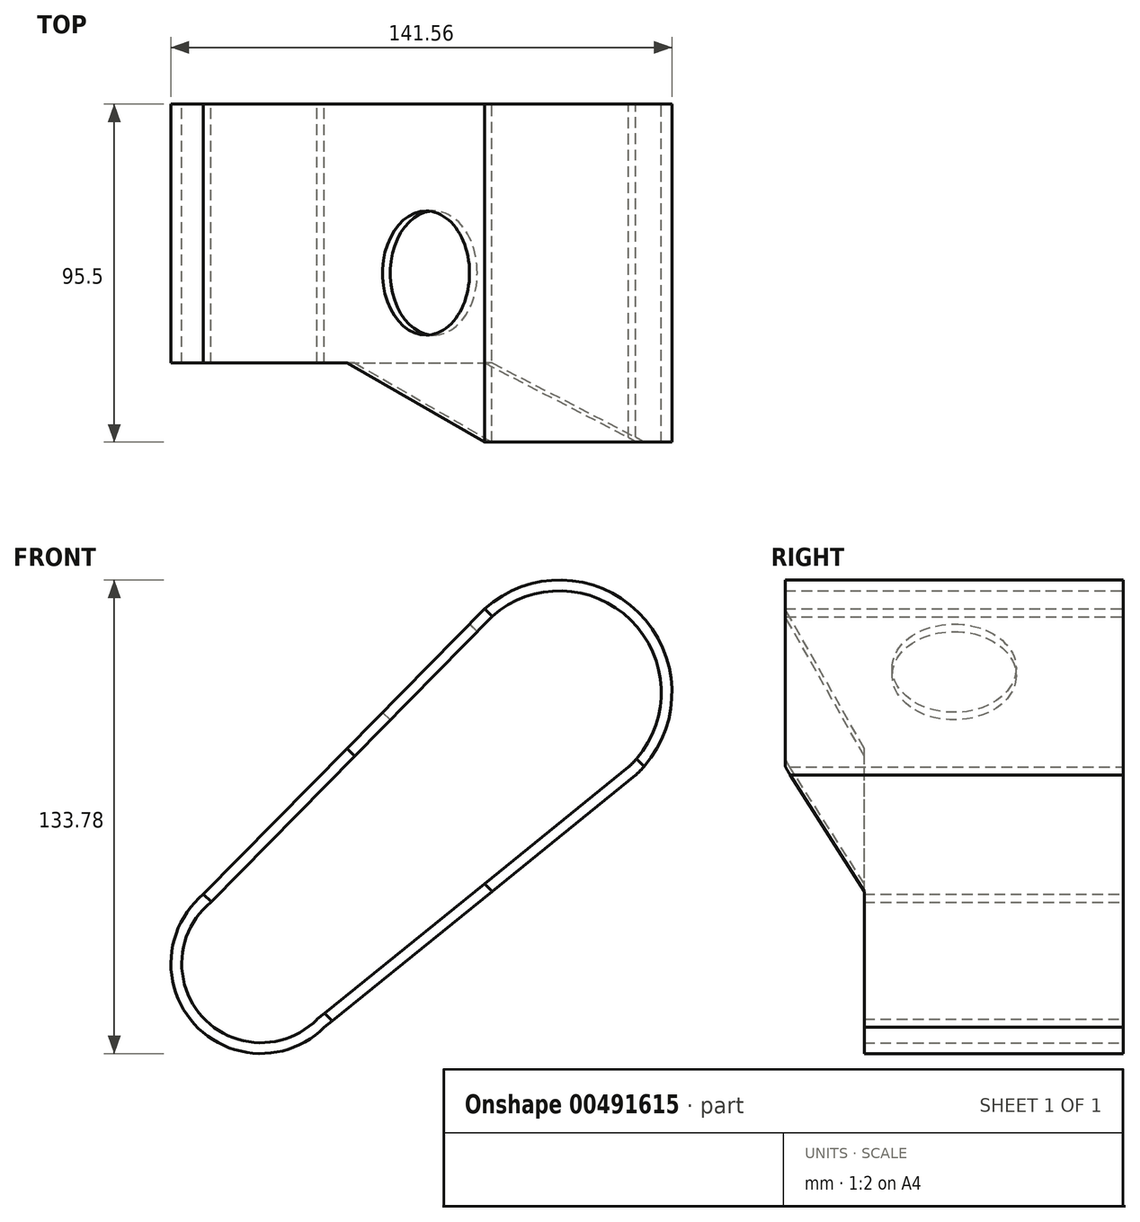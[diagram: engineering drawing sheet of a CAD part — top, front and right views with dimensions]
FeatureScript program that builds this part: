
annotation { "Feature Type Name" : "Feature", "Feature Type Description" : "" }
export const myFeature = defineFeature(function(context is Context, id is Id, definition is map)
    precondition{}
    {
        {
            var Q0;
            Q0=qCreatedBy(makeId("Front.planeOp"),FACE);
            var sketch = newSketch(context, id + "F0", { "sketchPlane" : qUnion([Q0])});
            skPoint(sketch, "E0.visualSharp", {"position": v(-73.61, -25.13) * mm});
            skPoint(sketch, "E1.visualSharp", {"position": v(-33.06, -65.08) * mm});
            skPoint(sketch, "E2.visualSharp", {"position": v(65.09, 34.55) * mm});
            skPoint(sketch, "E3.visualSharp", {"position": v(24.53, 74.5) * mm});
            skArc(sketch, "E4.1", {"start": v(-27.4, -54.87) * mm, "mid": v(-64.13, -53.94) * mm, "end": v(-61.56, -17.28) * mm});
            skArc(sketch, "E4.5", {"start": v(17.82, 63.36) * mm, "mid": v(62.56, 61.12) * mm, "end": v(60.53, 16.37) * mm});
            skLineSegment(sketch, "E5", {"start": v(-61.56, -17.28) * mm, "end": v(17.82, 63.36) * mm});
            skLineSegment(sketch, "E6", {"start": v(-27.4, -54.87) * mm, "end": v(60.53, 16.37) * mm});
            skLineSegment(sketch, "E7.0", {"start": v(-59.5, -19.53) * mm, "end": v(19.93, 61.15) * mm});
            skArc(sketch, "E7.1", {"start": v(-29.43, -52.6) * mm, "mid": v(-61.88, -51.9) * mm, "end": v(-59.5, -19.53) * mm});
            skLineSegment(sketch, "E7.2", {"start": v(-29.43, -52.6) * mm, "end": v(58.54, 18.68) * mm});
            skArc(sketch, "E7.3", {"start": v(19.93, 61.15) * mm, "mid": v(60.3, 59.07) * mm, "end": v(58.54, 18.68) * mm});
            skLineSegment(sketch, "E8", {"start": v(-61.56, -17.28) * mm, "end": v(-21.87, 23.04) * mm});
            skLineSegment(sketch, "E9", {"start": v(-21.87, 23.04) * mm, "end": v(16.57, -19.25) * mm});
            skLineSegment(sketch, "E10", {"start": v(17.82, 63.36) * mm, "end": v(19.93, 61.15) * mm});
            skLineSegment(sketch, "E11", {"start": v(58.54, 18.68) * mm, "end": v(60.53, 16.37) * mm});
            skSolve(sketch);
        }
        {
            var Q0;
            Q0 = qSketchRegion(id + "F0", true);
            extrude(context, id + "F1", {"entities" : qUnion([Q0]), "endBound" : BoundingType.SYMMETRIC, "depth" : 95.5 * mm});
        }
        {
            var Q0;
            Q0=makeQuery(id+"F1.opExtrude","SWEPT_FACE",FACE,{"disambiguationData":[OSD([sQuery(id+"F0.wireOp",EDGE,"E5")])]});
            var sketch = newSketch(context, id + "F2", { "sketchPlane" : qUnion([Q0])});
            skLineSegment(sketch, "E12", {"start": v(47.75, 57.65) * mm, "end": v(47.75, 2.33) * mm});
            skLineSegment(sketch, "E13", {"start": v(25.4, 2.33) * mm, "end": v(47.75, 57.65) * mm});
            skLineSegment(sketch, "E14", {"start": v(25.4, -55.5) * mm, "end": v(25.4, 2.33) * mm});
            skLineSegment(sketch, "E15", {"start": v(25.4, -55.5) * mm, "end": v(25.4, -94.43) * mm});
            skLineSegment(sketch, "E16", {"start": v(25.4, -94.43) * mm, "end": v(47.75, -94.43) * mm});
            skLineSegment(sketch, "E17", {"start": v(47.75, -94.43) * mm, "end": v(47.75, -55.5) * mm});
            skCircle(sketch, "E18", {"center": v(0, 34.15) * mm, "radius": 17.52 * mm});
            skPoint(sketch, "E18.centerSnap0", {"position": v(0, 57.65) * mm});
            skSolve(sketch);
        }
        {
            var Q0;
            {var subQ4=sQuery(id+"F2.wireOp",EDGE,"E12");Q0=makeQuery(id+"F2.imprint","IMPRINT",FACE,{"disambiguationData":[TD([[makeQuery(id+"F2.imprint","IMPRINT",EDGE,{"derivedFrom":subQ4}),1.0]])]});}
            extrude(context, id + "F3", {"entities" : qUnion([Q0]), "operationType" : NewBodyOperationType.REMOVE, "endBound" : BoundingType.THROUGH_ALL, "oppositeDirection" : true, "depth" : 25.4 * mm});
        }
        {
            var Q0;
            Q0=makeQuery(id+"F1.opExtrude","SWEPT_FACE",FACE,{"disambiguationData":[OSD([sQuery(id+"F0.wireOp",EDGE,"E5"),sQuery(id+"F0.wireOp",EDGE,"E8")])]});
            cPlane(context, id + "F4", {"entities" : qUnion([Q0]), "cplaneType" : CPlaneType.OFFSET, "offset" : 2.54 * mm, "width" : 152.4 * mm, "height" : 152.4 * mm});
        }
        {
            var Q0;
            Q0=qCreatedBy(id+"F4.planeOp",FACE);
            var sketch = newSketch(context, id + "F5", { "sketchPlane" : qUnion([Q0])});
            skLineSegment(sketch, "E19.bottom", {"start": v(25.43, -54.43) * mm, "end": v(54, -54.43) * mm});
            skLineSegment(sketch, "E19.top", {"start": v(25.43, -133.75) * mm, "end": v(54, -133.75) * mm});
            skLineSegment(sketch, "E19.left", {"start": v(25.43, -54.43) * mm, "end": v(25.43, -133.75) * mm});
            skLineSegment(sketch, "E19.right", {"start": v(54, -54.43) * mm, "end": v(54, -133.75) * mm});
            skSolve(sketch);
        }
        {
            var Q0;
            Q0 = qSketchRegion(id + "F5", true);
            extrude(context, id + "F6", {"entities" : qUnion([Q0]), "operationType" : NewBodyOperationType.REMOVE, "endBound" : BoundingType.THROUGH_ALL, "oppositeDirection" : true, "depth" : 25.4 * mm});
        }
        {
            var Q0;
            Q0 = qSketchRegion(id + "F2", true);
            extrude(context, id + "F7", {"entities" : qUnion([Q0]), "operationType" : NewBodyOperationType.REMOVE, "endBound" : BoundingType.UP_TO_NEXT, "oppositeDirection" : true, "depth" : 25.4 * mm});
        }
    });
